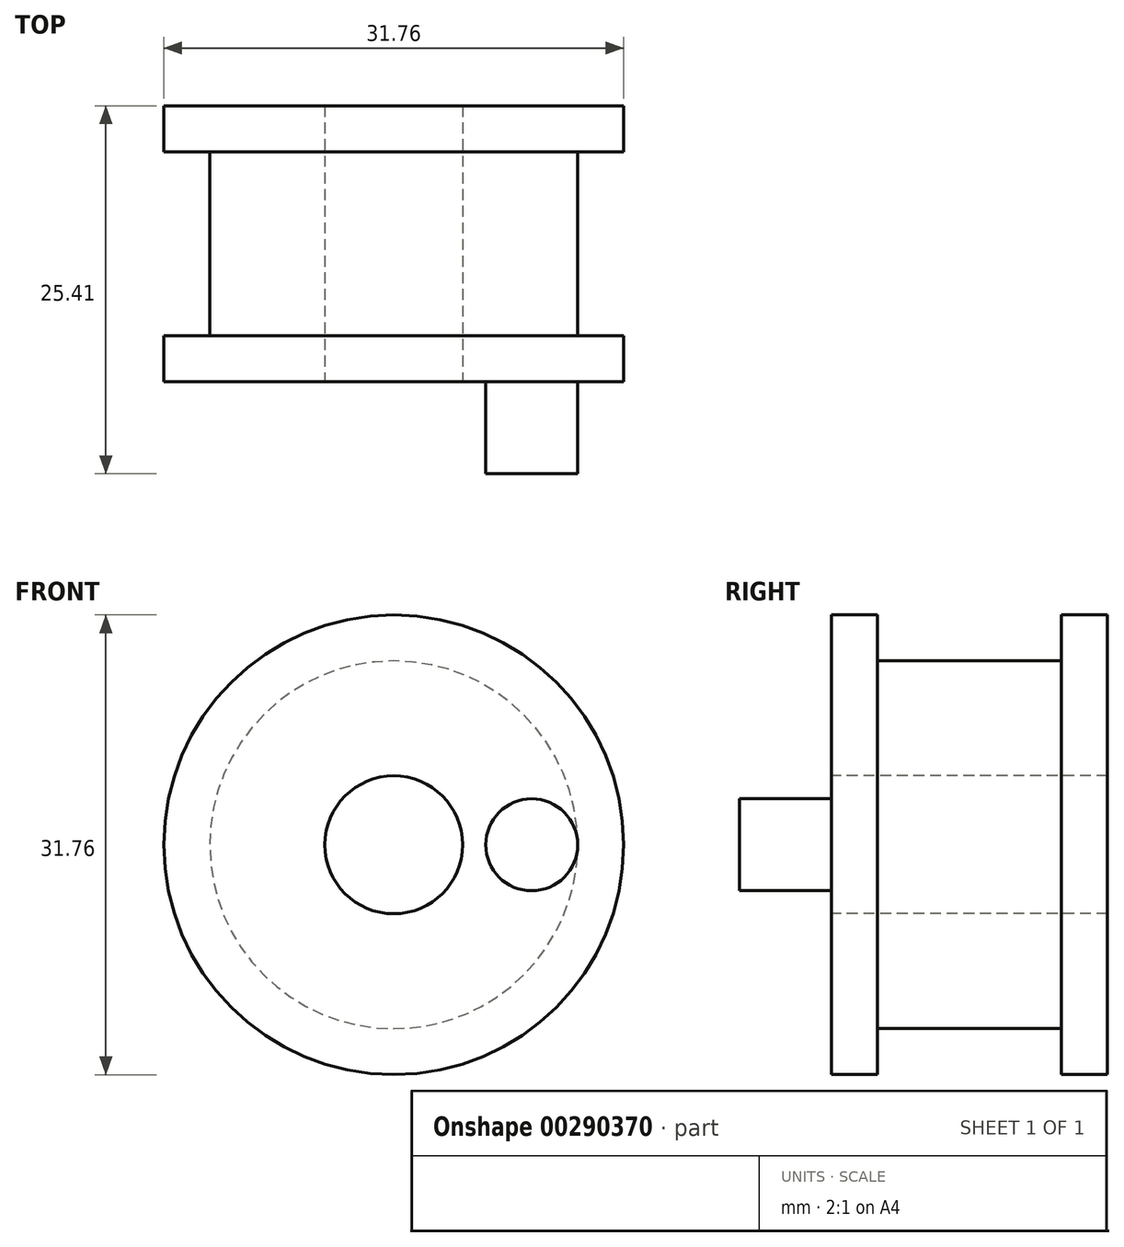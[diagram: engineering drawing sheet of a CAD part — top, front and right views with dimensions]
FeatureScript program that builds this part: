
annotation { "Feature Type Name" : "Feature", "Feature Type Description" : "" }
export const myFeature = defineFeature(function(context is Context, id is Id, definition is map)
    precondition{}
    {
        {
            var Q0;
            Q0=qCreatedBy(makeId("Right.planeOp"),FACE);
            var sketch = newSketch(context, id + "F0", { "sketchPlane" : qUnion([Q0])});
            skLineSegment(sketch, "E0.bottom", {"start": v(-6.35, 12.7) * mm, "end": v(6.35, 12.7) * mm});
            skLineSegment(sketch, "E0.top", {"start": v(-6.35, 4.76) * mm, "end": v(6.35, 4.76) * mm});
            skLineSegment(sketch, "E0.left", {"start": v(-6.35, 12.7) * mm, "end": v(-6.35, 4.76) * mm});
            skLineSegment(sketch, "E0.right", {"start": v(6.35, 12.7) * mm, "end": v(6.35, 4.76) * mm});
            skPoint(sketch, "E1", {"position": v(0, 4.76) * mm});
            skLineSegment(sketch, "E2.bottom", {"start": v(-9.53, 15.88) * mm, "end": v(-6.35, 15.88) * mm});
            skLineSegment(sketch, "E2.top", {"start": v(-9.53, 4.76) * mm, "end": v(9.53, 4.76) * mm});
            skLineSegment(sketch, "E2.left", {"start": v(-9.53, 15.88) * mm, "end": v(-9.53, 4.76) * mm});
            skLineSegment(sketch, "E2.right", {"start": v(9.52, 15.88) * mm, "end": v(9.53, 4.76) * mm});
            skPoint(sketch, "E3", {"position": v(-6.35, 15.88) * mm});
            skPoint(sketch, "E4", {"position": v(6.35, 15.88) * mm});
            skLineSegment(sketch, "E5.trimOffspring", {"start": v(6.35, 15.88) * mm, "end": v(9.52, 15.88) * mm});
            skLineSegment(sketch, "E6", {"start": v(-6.35, 15.88) * mm, "end": v(-6.35, 12.7) * mm});
            skLineSegment(sketch, "E7", {"start": v(6.35, 15.88) * mm, "end": v(6.35, 12.7) * mm});
            skLineSegment(sketch, "E8", {"start": v(-9.52, 0) * mm, "end": v(9.53, 0) * mm});
            skSolve(sketch);
        }
        {
            var Q0;
            Q0 = qSketchRegion(id + "F0", true);
            var Q1;
            Q1=sQuery(id+"F0.wireOp",EDGE,"E8");
            revolve(context, id + "F1", {"entities" : qUnion([Q0]), "axis" : qUnion([Q1]), "revolveType" : RevolveType.FULL});
        }
        {
            var Q0;
            Q0=makeQuery(id+"F1.opRevolve","SWEPT_FACE",FACE,{"disambiguationData":[OSD([sQuery(id+"F0.wireOp",EDGE,"E2.left")])]});
            var sketch = newSketch(context, id + "F2", { "sketchPlane" : qUnion([Q0])});
            skCircle(sketch, "E9", {"center": v(9.53, 0) * mm, "radius": 3.18 * mm});
            skSolve(sketch);
        }
        {
            var Q0;
            Q0 = qSketchRegion(id + "F2", true);
            extrude(context, id + "F3", {"entities" : qUnion([Q0]), "operationType" : NewBodyOperationType.ADD, "depth" : 6.35 * mm});
        }
    });
